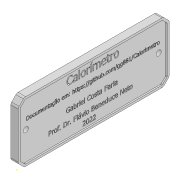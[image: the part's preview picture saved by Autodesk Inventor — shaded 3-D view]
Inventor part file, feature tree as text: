
AUTODESK INVENTOR PART (.ipt)
format: ipt  version: 2020 (Build 240168000, 168)  size: 3,535,360 bytes
history: native  units: mm
features: sketch x5, extrude x4, other x2, chamfer x1, fillet x1
ambient origin geometry x8: Origin, YZ Plane, XZ Plane, XY Plane, X Axis, Y Axis, Z Axis, Center Point
bodies: Body1 (feature_tree)
feature tree (13):
  other  "Sólido1"
  extrude  "Extrusão1"  Depth=100.0mm
  extrude  "Extrusão2"  Depth=3.5mm
  extrude  "Extrusão3"  Depth=6.0mm
  chamfer  "Chanfro1"  Distance=4.0mm
  fillet  "Arredondamento1"  Radius=40.0mm
  sketch  "Esboço4"  dims[d7=6.0mm d8=4.0mm d9=0.0mm d10=40.0mm]
  sketch  "Esboço5"  dims[d11=20.0mm d12=20.0mm d13=1.0mm d14=0.0mm d15=4.0mm d16=2.0mm d17=45.0deg d18=2.0mm d19=1.0mm d20=0.0mm]
  extrude  "Extrusão4"  Depth=1.0mm
  sketch  "Esboço1"  dims[d0=100.0mm d1=40.0mm]
  sketch  "Esboço2"  dims[d2=4.0mm d3=0.0mm d4=3.5mm]
  sketch  "Esboço3"  dims[d5=3.5mm d6=6.0mm]
  other  "Contorno projetado1"
